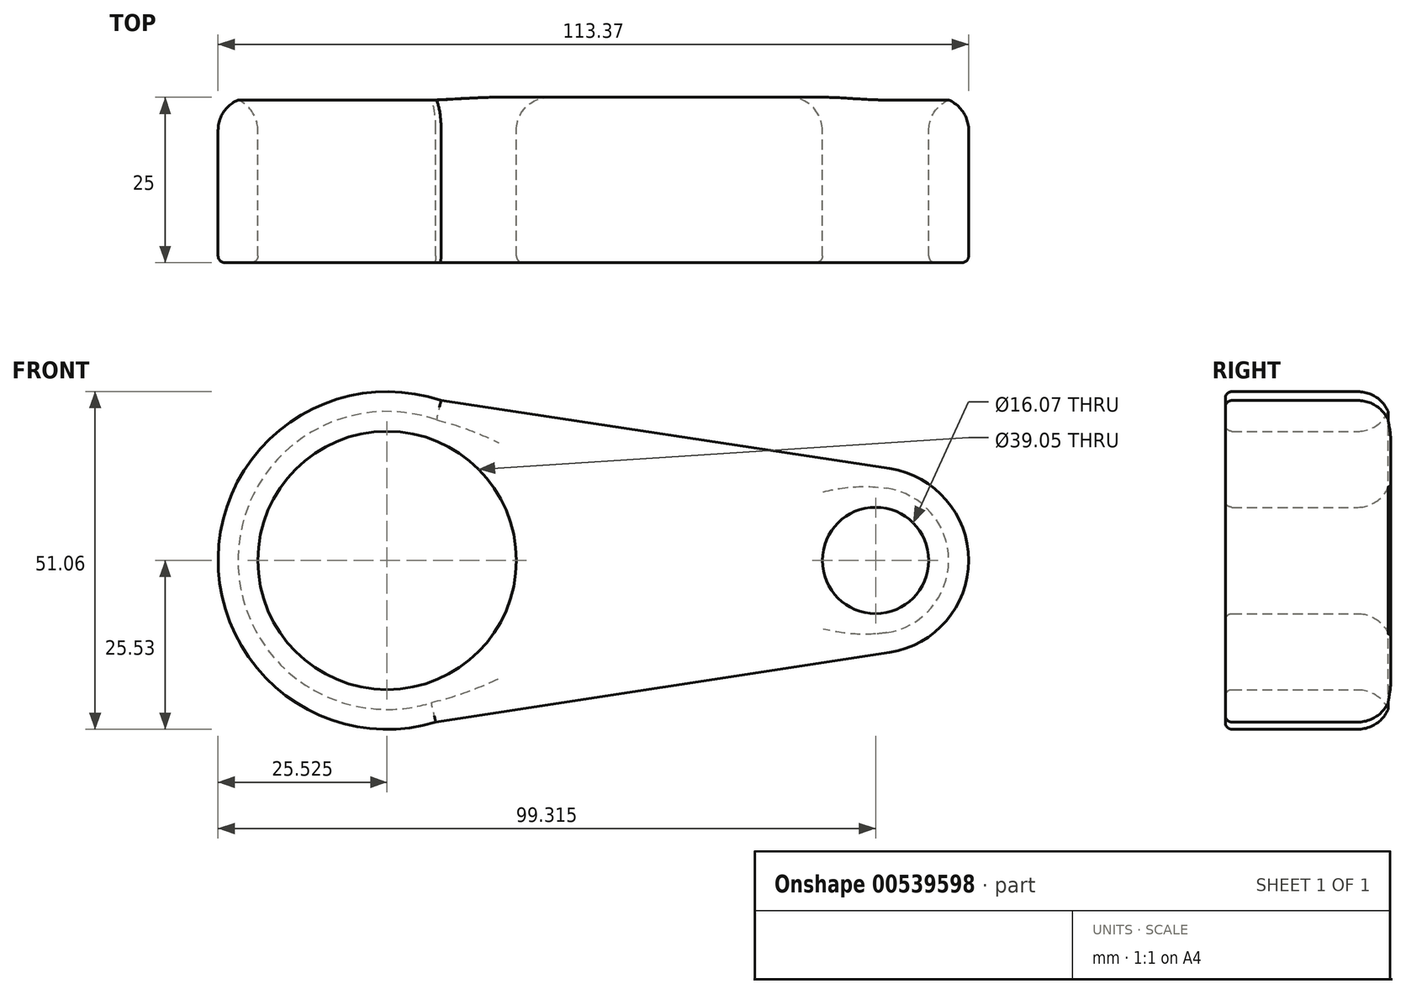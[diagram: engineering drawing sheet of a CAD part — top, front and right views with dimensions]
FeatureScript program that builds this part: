
annotation { "Feature Type Name" : "Feature", "Feature Type Description" : "" }
export const myFeature = defineFeature(function(context is Context, id is Id, definition is map)
    precondition{}
    {
        {
            var Q0;
            Q0=qCreatedBy(makeId("Front.planeOp"),FACE);
            var sketch = newSketch(context, id + "F0", { "sketchPlane" : qUnion([Q0])});
            skCircle(sketch, "E0", {"center": v(-36.9, 0) * mm, "radius": 25.53 * mm});
            skCircle(sketch, "E1", {"center": v(36.9, 0) * mm, "radius": 14.06 * mm});
            skLineSegment(sketch, "E2", {"start": v(-37.5, 25.52) * mm, "end": v(39, 13.9) * mm});
            skLineSegment(sketch, "E3", {"start": v(-36.57, -25.52) * mm, "end": v(39.03, -13.9) * mm});
            skCircle(sketch, "E4", {"center": v(-36.9, 0) * mm, "radius": 19.52 * mm});
            skCircle(sketch, "E5", {"center": v(36.9, 0) * mm, "radius": 8.04 * mm});
            skSolve(sketch);
        }
        {
            var Q0;
            Q0 = qSketchRegion(id + "F0", true);
            extrude(context, id + "F1", {"entities" : qUnion([Q0]), "depth" : 25 * mm, "offsetDistance" : 25 * mm});
        }
        {
            var Q0;
            Q0=makeQuery(id+"F1.opExtrude","CAP_EDGE",EDGE,{"disambiguationData":[OSD([sQuery(id+"F0.wireOp",EDGE,"E2")])],"isStart":false});
            var Q1;
            Q1=makeQuery(id+"F1.opExtrude","CAP_EDGE",EDGE,{"disambiguationData":[OSD([sQuery(id+"F0.wireOp",EDGE,"E0")])],"isStart":false});
            var Q2;
            Q2=makeQuery(id+"F1.opExtrude","CAP_EDGE",EDGE,{"disambiguationData":[OSD([sQuery(id+"F0.wireOp",EDGE,"E4")])],"isStart":false});
            var Q3;
            Q3=makeQuery(id+"F1.opExtrude","CAP_EDGE",EDGE,{"disambiguationData":[OSD([sQuery(id+"F0.wireOp",EDGE,"E5")])],"isStart":false});
            fillet(context, id + "F2", {"entities" : qUnion([Q0, Q1, Q2, Q3]), "radius" : 1 * mm, "tangentPropagation" : true, "allowEdgeOverflow" : false});
        }
        {
            var Q0;
            Q0=makeQuery(id+"F1.opExtrude","CAP_FACE",FACE,{"disambiguationData":[OSD([sQuery(id+"F0.wireOp",EDGE,"E0"),sQuery(id+"F0.wireOp",EDGE,"E1"),sQuery(id+"F0.wireOp",EDGE,"E2"),sQuery(id+"F0.wireOp",EDGE,"E3"),sQuery(id+"F0.wireOp",EDGE,"E4"),sQuery(id+"F0.wireOp",EDGE,"E5")])],"isStart":true});
            var Q1;
            Q1=makeQuery(id+"F1.opExtrude","CAP_EDGE",EDGE,{"disambiguationData":[OSD([sQuery(id+"F0.wireOp",EDGE,"E5")])],"isStart":true});
            var Q2;
            Q2=makeQuery(id+"F1.opExtrude","CAP_EDGE",EDGE,{"disambiguationData":[OSD([sQuery(id+"F0.wireOp",EDGE,"E1")])],"isStart":true});
            var Q3;
            Q3=makeQuery(id+"F1.opExtrude","CAP_EDGE",EDGE,{"disambiguationData":[OSD([sQuery(id+"F0.wireOp",EDGE,"E2")])],"isStart":true});
            var Q4;
            {var subQ0=sQuery(id+"F0.wireOp",EDGE,"E4");Q4=makeQuery(id+"F2.opFillet","BLEND_EDGE",EDGE,{"blendedFrom":[makeQuery(id+"F1.opExtrude","CAP_EDGE",EDGE,{"disambiguationData":[OSD([subQ0])],"isStart":false}),makeQuery(id+"F1.opExtrude","SWEPT_FACE",FACE,{"disambiguationData":[OSD([subQ0])]})],"blendedInto":[makeQuery(id+"F1.opExtrude","SWEPT_FACE",FACE,{"disambiguationData":[OSD([subQ0])]})]});}
            var Q5;
            {var subQ0=sQuery(id+"F0.wireOp",EDGE,"E5");Q5=makeQuery(id+"F2.opFillet","BLEND_EDGE",EDGE,{"blendedFrom":[makeQuery(id+"F1.opExtrude","CAP_EDGE",EDGE,{"disambiguationData":[OSD([subQ0])],"isStart":false}),makeQuery(id+"F1.opExtrude","SWEPT_FACE",FACE,{"disambiguationData":[OSD([subQ0])]})],"blendedInto":[makeQuery(id+"F1.opExtrude","SWEPT_FACE",FACE,{"disambiguationData":[OSD([subQ0])]})]});}
            var Q6;
            {var subQ0=sQuery(id+"F0.wireOp",EDGE,"E0");Q6=makeQuery(id+"F2.opFillet","BLEND_EDGE",EDGE,{"blendedFrom":[makeQuery(id+"F1.opExtrude","CAP_EDGE",EDGE,{"disambiguationData":[OSD([subQ0])],"isStart":false}),makeQuery(id+"F1.opExtrude","CAP_FACE",FACE,{"disambiguationData":[OSD([subQ0,sQuery(id+"F0.wireOp",EDGE,"E1"),sQuery(id+"F0.wireOp",EDGE,"E2"),sQuery(id+"F0.wireOp",EDGE,"E3"),sQuery(id+"F0.wireOp",EDGE,"E4"),sQuery(id+"F0.wireOp",EDGE,"E5")])],"isStart":false})],"blendedInto":[makeQuery(id+"F1.opExtrude","CAP_FACE",FACE,{"disambiguationData":[OSD([subQ0,sQuery(id+"F0.wireOp",EDGE,"E1"),sQuery(id+"F0.wireOp",EDGE,"E2"),sQuery(id+"F0.wireOp",EDGE,"E3"),sQuery(id+"F0.wireOp",EDGE,"E4"),sQuery(id+"F0.wireOp",EDGE,"E5")])],"isStart":false})]});}
            var Q7;
            {var subQ0=sQuery(id+"F0.wireOp",EDGE,"E0");Q7=makeQuery(id+"F2.opFillet","BLEND_EDGE",EDGE,{"blendedFrom":[makeQuery(id+"F1.opExtrude","CAP_EDGE",EDGE,{"disambiguationData":[OSD([subQ0])],"isStart":false}),makeQuery(id+"F1.opExtrude","CAP_FACE",FACE,{"disambiguationData":[OSD([subQ0,sQuery(id+"F0.wireOp",EDGE,"E1"),sQuery(id+"F0.wireOp",EDGE,"E2"),sQuery(id+"F0.wireOp",EDGE,"E3"),sQuery(id+"F0.wireOp",EDGE,"E4"),sQuery(id+"F0.wireOp",EDGE,"E5")])],"isStart":false})],"blendedInto":[makeQuery(id+"F1.opExtrude","CAP_FACE",FACE,{"disambiguationData":[OSD([subQ0,sQuery(id+"F0.wireOp",EDGE,"E1"),sQuery(id+"F0.wireOp",EDGE,"E2"),sQuery(id+"F0.wireOp",EDGE,"E3"),sQuery(id+"F0.wireOp",EDGE,"E4"),sQuery(id+"F0.wireOp",EDGE,"E5")])],"isStart":false})]});}
            var Q8;
            {var subQ0=sQuery(id+"F0.wireOp",EDGE,"E3");Q8=makeQuery(id+"F2.opFillet","BLEND_EDGE",EDGE,{"blendedFrom":[makeQuery(id+"F1.opExtrude","CAP_EDGE",EDGE,{"disambiguationData":[OSD([subQ0])],"isStart":false}),makeQuery(id+"F1.opExtrude","SWEPT_FACE",FACE,{"disambiguationData":[OSD([subQ0])]})],"blendedInto":[makeQuery(id+"F1.opExtrude","SWEPT_FACE",FACE,{"disambiguationData":[OSD([subQ0])]})]});}
            var Q9;
            {var subQ0=sQuery(id+"F0.wireOp",EDGE,"E1");Q9=makeQuery(id+"F2.opFillet","BLEND_EDGE",EDGE,{"blendedFrom":[makeQuery(id+"F1.opExtrude","CAP_EDGE",EDGE,{"disambiguationData":[OSD([subQ0])],"isStart":false}),makeQuery(id+"F1.opExtrude","SWEPT_FACE",FACE,{"disambiguationData":[OSD([subQ0])]})],"blendedInto":[makeQuery(id+"F1.opExtrude","SWEPT_FACE",FACE,{"disambiguationData":[OSD([subQ0])]})]});}
            fillet(context, id + "F3", {"entities" : qUnion([Q0, Q1, Q2, Q3, Q4, Q5, Q6, Q7, Q8, Q9]), "radius" : 5 * mm, "tangentPropagation" : true, "allowEdgeOverflow" : false});
        }
    });
